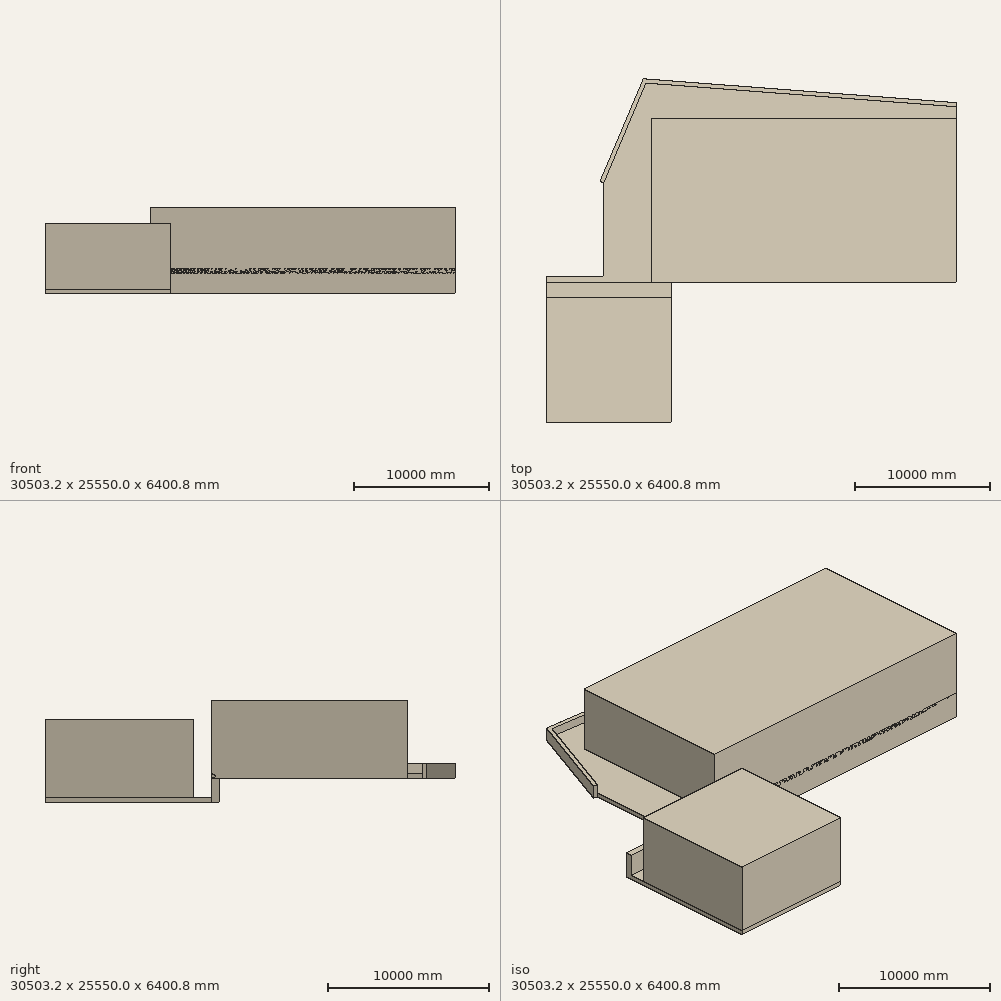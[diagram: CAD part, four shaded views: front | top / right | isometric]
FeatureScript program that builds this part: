
annotation { "Feature Type Name" : "Feature", "Feature Type Description" : "" }
export const myFeature = defineFeature(function(context is Context, id is Id, definition is map)
    precondition{}
    {
        {
            var Q0;
            Q0=qCreatedBy(makeId("Top.planeOp"),FACE);
            var sketch = newSketch(context, id + "F0", { "sketchPlane" : qUnion([Q0])});
            skPoint(sketch, "E0", {"position": v(-23068.74, 13037.45) * mm});
            skPoint(sketch, "E1", {"position": v(-26212.8, 5597.29) * mm});
            skPoint(sketch, "E2", {"position": v(-26212.8, 0) * mm});
            skPoint(sketch, "E3", {"position": v(0, 0) * mm});
            skPoint(sketch, "E4", {"position": v(-30480, -1828.8) * mm});
            skPoint(sketch, "E5", {"position": v(-30480, -12192) * mm});
            skPoint(sketch, "E6", {"position": v(-21196.3, -12192) * mm});
            skLineSegment(sketch, "E7", {"start": v(0, 0) * mm, "end": v(0, 11277.6) * mm});
            skLineSegment(sketch, "E8", {"start": v(0, 11277.6) * mm, "end": v(-23068.74, 13037.45) * mm});
            skLineSegment(sketch, "E9", {"start": v(0, 0) * mm, "end": v(-26212.8, 0) * mm});
            skLineSegment(sketch, "E10", {"start": v(-26212.8, 5597.29) * mm, "end": v(-26212.8, 0) * mm});
            skLineSegment(sketch, "E11", {"start": v(-26212.8, 5597.29) * mm, "end": v(-23068.74, 13037.45) * mm});
            skLineSegment(sketch, "E12", {"start": v(-21196.3, -1828.8) * mm, "end": v(-21196.3, -12192) * mm});
            skLineSegment(sketch, "E13", {"start": v(-30480, -12192) * mm, "end": v(-21196.3, -12192) * mm});
            skLineSegment(sketch, "E14", {"start": v(-30480, -1828.8) * mm, "end": v(-30480, -12192) * mm});
            skLineSegment(sketch, "E15", {"start": v(-30480, -1828.8) * mm, "end": v(-21196.3, -1828.8) * mm});
            skLineSegment(sketch, "E16", {"start": v(-21196.3, -1828.8) * mm, "end": v(0, -1828.8) * mm});
            skLineSegment(sketch, "E17", {"start": v(0, -1828.8) * mm, "end": v(0, 0) * mm});
            skLineSegment(sketch, "E18", {"start": v(-30480, -1371.6) * mm, "end": v(-30480, -1828.8) * mm});
            skPoint(sketch, "E19", {"position": v(-30480, -1371.6) * mm});
            skPoint(sketch, "E20", {"position": v(0, -1371.6) * mm});
            skLineSegment(sketch, "E21", {"start": v(-30480, -1371.6) * mm, "end": v(0, -1371.6) * mm});
            skLineSegment(sketch, "E22.0", {"start": v(23.19, 11581.52) * mm, "end": v(-23264.16, 13358.05) * mm});
            skLineSegment(sketch, "E22.1", {"start": v(-26493.56, 5715.93) * mm, "end": v(-23264.16, 13358.05) * mm});
            skLineSegment(sketch, "E23", {"start": v(23.19, 11581.52) * mm, "end": v(0, 11277.6) * mm});
            skLineSegment(sketch, "E24", {"start": v(-26493.56, 5715.93) * mm, "end": v(-26212.8, 5597.29) * mm});
            skLineSegment(sketch, "E25", {"start": v(-26212.8, 0) * mm, "end": v(-26212.8, -1371.6) * mm});
            skLineSegment(sketch, "E26", {"start": v(0, 10394.95) * mm, "end": v(-22694.9, 10394.95) * mm});
            skLineSegment(sketch, "E27", {"start": v(-22694.9, 10394.95) * mm, "end": v(-22694.9, -1371.6) * mm});
            skLineSegment(sketch, "E28", {"start": v(-30480, -2946.4) * mm, "end": v(-21196.3, -2946.4) * mm});
            skLineSegment(sketch, "E29", {"start": v(-22694.9, -1371.6) * mm, "end": v(-22694.9, -1828.8) * mm});
            skSolve(sketch);
        }
        {
            var Q0;
            Q0=makeQuery(id+"F0.imprint","IMPRINT",FACE,{"disambiguationData":[TD([[makeQuery(id+"F0.imprint","IMPRINT",EDGE,{"derivedFrom":sQuery(id+"F0.wireOp",EDGE,"E8")}),-1.0]])]});
            extrude(context, id + "F1", {"entities" : qUnion([Q0]), "depth" : 914.4 * mm, "offsetDistance" : 30.48 * mm});
        }
        {
            var Q0;
            Q0=makeQuery(id+"F0.imprint","IMPRINT",FACE,{"disambiguationData":[TD([[makeQuery(id+"F0.imprint","IMPRINT",EDGE,{"derivedFrom":sQuery(id+"F0.wireOp",EDGE,"E7")}),1.0]])]});
            var Q1;
            {var subQ3=sQuery(id+"F0.wireOp",EDGE,"E9");Q1=makeQuery(id+"F0.imprint","IMPRINT",FACE,{"disambiguationData":[TD([[makeQuery(id+"F0.imprint","IMPRINT",EDGE,{"derivedFrom":subQ3}),1.0]])]});}
            var Q2;
            {var subQ4=sQuery(id+"F0.wireOp",EDGE,"E15");Q2=makeQuery(id+"F0.imprint","IMPRINT",FACE,{"disambiguationData":[TD([[makeQuery(id+"F0.imprint","IMPRINT",EDGE,{"derivedFrom":subQ4}),1.0]])]});}
            var Q3;
            {var subQ0=sQuery(id+"F0.wireOp",EDGE,"E10");Q3=makeQuery(id+"F0.imprint","IMPRINT",FACE,{"disambiguationData":[TD([[makeQuery(id+"F0.imprint","IMPRINT",EDGE,{"derivedFrom":subQ0}),1.0]])]});}
            extrude(context, id + "F2", {"entities" : qUnion([Q0, Q1, Q2, Q3]), "operationType" : NewBodyOperationType.ADD, "depth" : 304.8 * mm, "offsetDistance" : 30.48 * mm});
        }
        {
            var Q0;
            {var subQ4=sQuery(id+"F0.wireOp",EDGE,"E15");Q0=makeQuery(id+"F0.imprint","IMPRINT",FACE,{"disambiguationData":[TD([[makeQuery(id+"F0.imprint","IMPRINT",EDGE,{"derivedFrom":subQ4}),1.0]])]});}
            extrude(context, id + "F3", {"entities" : qUnion([Q0]), "operationType" : NewBodyOperationType.ADD, "oppositeDirection" : true, "depth" : 1524 * mm, "offsetDistance" : 30.48 * mm});
        }
        {
            var Q0;
            Q0=makeQuery(id+"F0.imprint","IMPRINT",FACE,{"disambiguationData":[TD([[makeQuery(id+"F0.imprint","IMPRINT",EDGE,{"derivedFrom":sQuery(id+"F0.wireOp",EDGE,"E12")}),-1.0]])]});
            var Q1;
            {var subQ6=sQuery(id+"F0.wireOp",EDGE,"E28");Q1=makeQuery(id+"F0.imprint","IMPRINT",FACE,{"disambiguationData":[TD([[makeQuery(id+"F0.imprint","IMPRINT",EDGE,{"derivedFrom":subQ6}),1.0]])]});}
            extrude(context, id + "F4", {"entities" : qUnion([Q0, Q1]), "operationType" : NewBodyOperationType.ADD, "oppositeDirection" : true, "depth" : 1524 * mm, "offsetDistance" : 30.48 * mm});
        }
        {
            var Q0;
            Q0=makeQuery(id+"F0.imprint","IMPRINT",FACE,{"disambiguationData":[TD([[makeQuery(id+"F0.imprint","IMPRINT",EDGE,{"derivedFrom":sQuery(id+"F0.wireOp",EDGE,"E12")}),-1.0]])]});
            var Q1;
            {var subQ6=sQuery(id+"F0.wireOp",EDGE,"E28");Q1=makeQuery(id+"F0.imprint","IMPRINT",FACE,{"disambiguationData":[TD([[makeQuery(id+"F0.imprint","IMPRINT",EDGE,{"derivedFrom":subQ6}),1.0]])]});}
            extrude(context, id + "F5", {"entities" : qUnion([Q0, Q1]), "operationType" : NewBodyOperationType.REMOVE, "oppositeDirection" : true, "depth" : 1219.2 * mm, "offsetDistance" : 30.48 * mm});
        }
        {
            var Q0;
            {var subQ0=sQuery(id+"F0.wireOp",EDGE,"E17");var subQ5=sQuery(id+"F0.wireOp",EDGE,"E21");var subQ6=makeQuery(id+"F0.imprint","INTERSECT",VERTEX,{"derivedFrom":[subQ0,subQ5]});Q0=makeQuery(id+"F0.imprint","IMPRINT",FACE,{"disambiguationData":[TD([[makeQuery(id+"F0.imprint","IMPRINT",EDGE,{"disambiguationData":[TD([[subQ6,1.0]])],"derivedFrom":subQ5}),1.0]])]});}
            var Q1;
            {var subQ3=sQuery(id+"F0.wireOp",EDGE,"E26");Q1=makeQuery(id+"F0.imprint","IMPRINT",FACE,{"disambiguationData":[TD([[makeQuery(id+"F0.imprint","IMPRINT",EDGE,{"derivedFrom":subQ3}),1.0]])]});}
            var Q2;
            {var subQ4=sQuery(id+"F0.wireOp",EDGE,"E16");Q2=makeQuery(id+"F0.imprint","IMPRINT",FACE,{"disambiguationData":[TD([[makeQuery(id+"F0.imprint","IMPRINT",EDGE,{"derivedFrom":subQ4}),1.0]])]});}
            extrude(context, id + "F6", {"entities" : qUnion([Q0, Q1, Q2]), "depth" : 4876.8 * mm, "offsetDistance" : 30.48 * mm});
        }
        {
            var Q0;
            {var subQ0=sQuery(id+"F0.wireOp",EDGE,"E13");Q0=makeQuery(id+"F0.imprint","IMPRINT",FACE,{"disambiguationData":[TD([[makeQuery(id+"F0.imprint","IMPRINT",EDGE,{"derivedFrom":subQ0}),1.0]])]});}
            var Q1;
            Q1=makeQuery(id+"F5.boolean.opBoolean","COPY",FACE,{"derivedFrom":makeQuery(id+"F5.opExtrude","CAP_FACE",FACE,{"disambiguationData":[OSD([sQuery(id+"F0.wireOp",EDGE,"E12"),sQuery(id+"F0.wireOp",EDGE,"E13"),sQuery(id+"F0.wireOp",EDGE,"E14"),sQuery(id+"F0.wireOp",EDGE,"E15")])],"isStart":false})});
            extrude(context, id + "F7", {"entities" : qUnion([Q0]), "endBound" : BoundingType.UP_TO_SURFACE, "oppositeDirection" : true, "depth" : 30.48 * mm, "endBoundEntityFace" : qUnion([Q1]), "offsetDistance" : 30.48 * mm});
        }
        {
            var Q0;
            {var subQ0=sQuery(id+"F0.wireOp",EDGE,"E13");Q0=makeQuery(id+"F0.imprint","IMPRINT",FACE,{"disambiguationData":[TD([[makeQuery(id+"F0.imprint","IMPRINT",EDGE,{"derivedFrom":subQ0}),1.0]])]});}
            extrude(context, id + "F8", {"entities" : qUnion([Q0]), "operationType" : NewBodyOperationType.ADD, "depth" : 3657.6 * mm, "offsetDistance" : 30.48 * mm});
        }
    });
